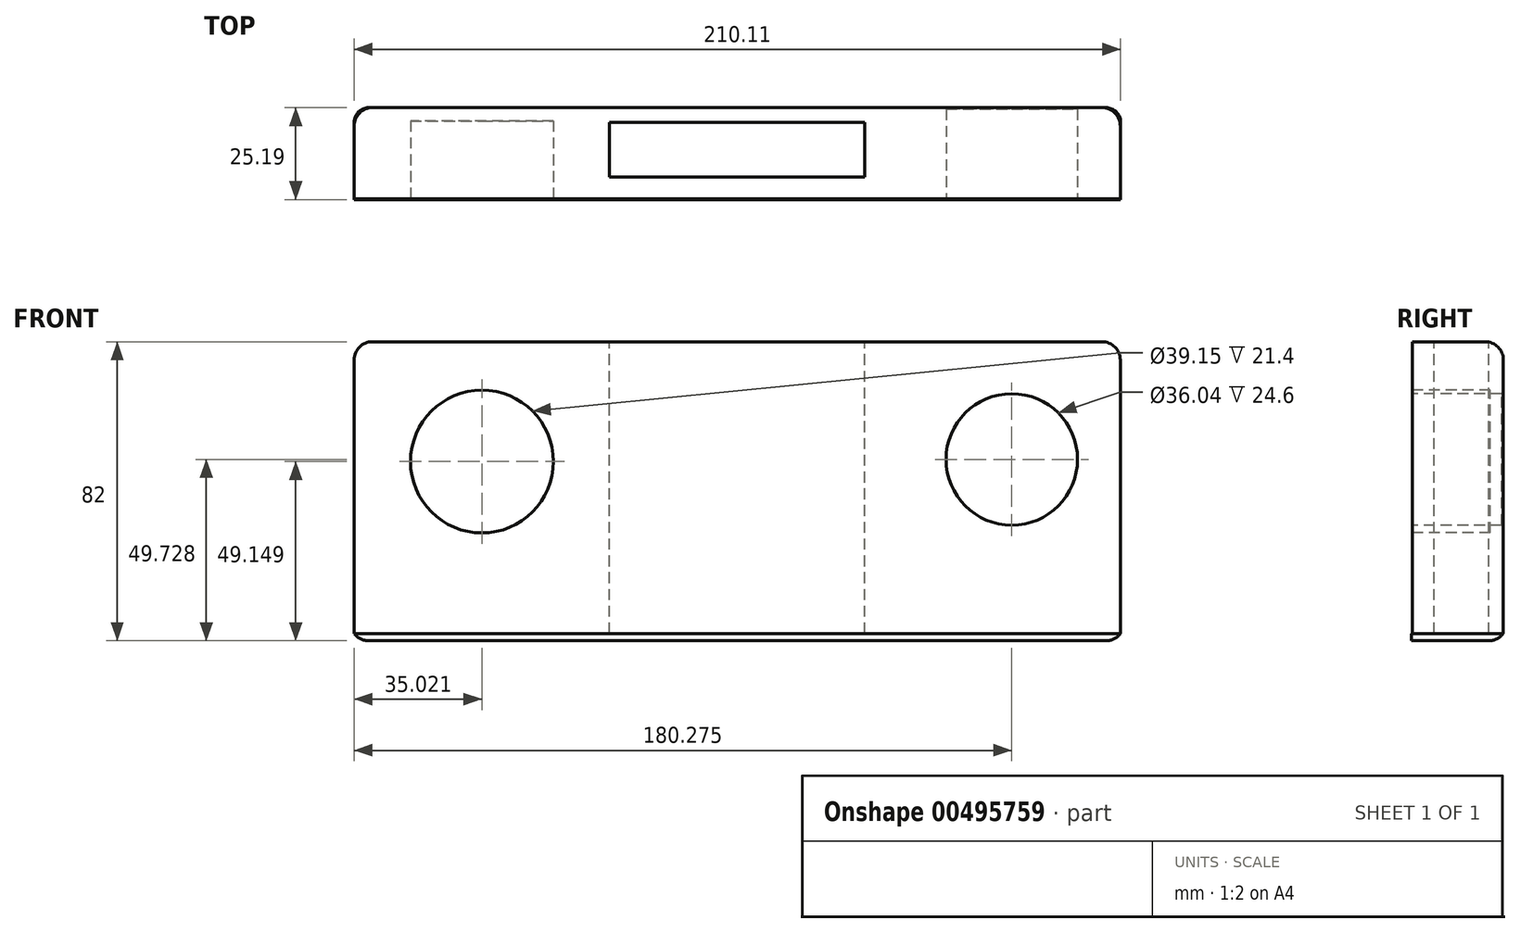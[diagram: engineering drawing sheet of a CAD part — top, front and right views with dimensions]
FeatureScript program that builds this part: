
annotation { "Feature Type Name" : "Feature", "Feature Type Description" : "" }
export const myFeature = defineFeature(function(context is Context, id is Id, definition is map)
    precondition{}
    {
        {
            var Q0;
            Q0=qCreatedBy(makeId("Front.planeOp"),FACE);
            var sketch = newSketch(context, id + "F0", { "sketchPlane" : qUnion([Q0])});
            skLineSegment(sketch, "E0.bottom", {"start": v(-105, 40) * mm, "end": v(105, 40) * mm});
            skLineSegment(sketch, "E0.top", {"start": v(-105, -40) * mm, "end": v(105, -40) * mm});
            skLineSegment(sketch, "E0.left", {"start": v(-105, 40) * mm, "end": v(-105, -40) * mm});
            skLineSegment(sketch, "E0.right", {"start": v(105, 40) * mm, "end": v(105, -40) * mm});
            skPoint(sketch, "E0.middle", {"position": v(0, 0) * mm});
            skSolve(sketch);
        }
        {
            var Q0;
            Q0 = qSketchRegion(id + "F0", true);
            extrude(context, id + "F1", {"entities" : qUnion([Q0]), "depth" : 25 * mm});
        }
        {
            var Q0;
            Q0=makeQuery(id+"F1.opExtrude","SWEPT_FACE",FACE,{"disambiguationData":[OSD([sQuery(id+"F0.wireOp",EDGE,"E0.bottom")])]});
            var sketch = newSketch(context, id + "F2", { "sketchPlane" : qUnion([Q0])});
            skLineSegment(sketch, "E1.bottom", {"start": v(-35, -3.97) * mm, "end": v(35, -3.97) * mm});
            skLineSegment(sketch, "E1.top", {"start": v(-35, -18.97) * mm, "end": v(35, -18.97) * mm});
            skLineSegment(sketch, "E1.left", {"start": v(-35, -3.97) * mm, "end": v(-35, -18.97) * mm});
            skLineSegment(sketch, "E1.right", {"start": v(35, -3.97) * mm, "end": v(35, -18.97) * mm});
            skPoint(sketch, "E1.middle", {"position": v(0, -11.47) * mm});
            skPoint(sketch, "E1.middle.positionSnap0", {"position": v(0, 0) * mm});
            skPoint(sketch, "E1.centerSnap0", {"position": v(0, 0) * mm});
            skSolve(sketch);
        }
        {
            var Q0;
            Q0 = qSketchRegion(id + "F2", true);
            extrude(context, id + "F3", {"entities" : qUnion([Q0]), "operationType" : NewBodyOperationType.REMOVE, "oppositeDirection" : true, "depth" : 111.1 * mm});
        }
        {
            var Q0;
            Q0=makeQuery(id+"F1.opExtrude","SWEPT_FACE",FACE,{"disambiguationData":[OSD([sQuery(id+"F0.wireOp",EDGE,"E0.top")])]});
            var sketch = newSketch(context, id + "F4", { "sketchPlane" : qUnion([Q0])});
            skSolve(sketch);
        }
        {
            var Q0;
            Q0=makeQuery(id+"F1.opExtrude","CAP_FACE",FACE,{"disambiguationData":[OSD([sQuery(id+"F0.wireOp",EDGE,"E0.bottom"),sQuery(id+"F0.wireOp",EDGE,"E0.top"),sQuery(id+"F0.wireOp",EDGE,"E0.left"),sQuery(id+"F0.wireOp",EDGE,"E0.right")])],"isStart":false});
            var sketch = newSketch(context, id + "F5", { "sketchPlane" : qUnion([Q0])});
            skCircle(sketch, "E2", {"center": v(-69.98, 7.15) * mm, "radius": 19.57 * mm});
            skPoint(sketch, "E2.first.point", {"position": v(-84.96, -5.44) * mm});
            skPoint(sketch, "E2.second.point", {"position": v(-52.58, 16.12) * mm});
            skPoint(sketch, "E2.third.point", {"position": v(-57.55, -7.97) * mm});
            skSolve(sketch);
        }
        {
            var Q0;
            Q0 = qSketchRegion(id + "F5", true);
            extrude(context, id + "F6", {"entities" : qUnion([Q0]), "operationType" : NewBodyOperationType.REMOVE, "oppositeDirection" : true, "depth" : 21.4 * mm});
        }
        {
            var Q0;
            Q0=makeQuery(id+"F1.opExtrude","CAP_FACE",FACE,{"disambiguationData":[OSD([sQuery(id+"F0.wireOp",EDGE,"E0.bottom"),sQuery(id+"F0.wireOp",EDGE,"E0.top"),sQuery(id+"F0.wireOp",EDGE,"E0.left"),sQuery(id+"F0.wireOp",EDGE,"E0.right")])],"isStart":false});
            var sketch = newSketch(context, id + "F7", { "sketchPlane" : qUnion([Q0])});
            skCircle(sketch, "E3", {"center": v(75.27, 7.73) * mm, "radius": 18.02 * mm});
            skPoint(sketch, "E3.first.point", {"position": v(59, 0) * mm});
            skPoint(sketch, "E3.second.point", {"position": v(88.16, 20.33) * mm});
            skPoint(sketch, "E3.third.point", {"position": v(82.38, -8.83) * mm});
            skSolve(sketch);
        }
        {
            var Q0;
            Q0 = qSketchRegion(id + "F7", true);
            extrude(context, id + "F8", {"entities" : qUnion([Q0]), "operationType" : NewBodyOperationType.REMOVE, "oppositeDirection" : true, "depth" : 24.6 * mm});
        }
        {
            var Q0;
            {var subQ0=sQuery(id+"F0.wireOp",EDGE,"E0.top");Q0=makeQuery(id+"F4.imprint","IMPRINT",FACE,{"disambiguationData":[TD([[makeQuery(id+"F4.imprint","IMPRINT",EDGE,{"derivedFrom":makeQuery(id+"F1.opExtrude","CAP_EDGE",EDGE,{"disambiguationData":[OSD([subQ0])],"isStart":true})}),1.0]])]});}
            var sketch = newSketch(context, id + "F9", { "sketchPlane" : qUnion([Q0])});
            skLineSegment(sketch, "E4.bottom", {"start": v(-104.98, 25.2) * mm, "end": v(105.11, 25.2) * mm});
            skLineSegment(sketch, "E4.top", {"start": v(-104.98, 0) * mm, "end": v(105.11, 0) * mm});
            skLineSegment(sketch, "E4.left", {"start": v(-104.98, 25.2) * mm, "end": v(-104.98, 0) * mm});
            skLineSegment(sketch, "E4.right", {"start": v(105.11, 25.2) * mm, "end": v(105.11, 0) * mm});
            skSolve(sketch);
        }
        {
            var Q0;
            Q0 = qSketchRegion(id + "F9", true);
            extrude(context, id + "F10", {"entities" : qUnion([Q0]), "depth" : 2 * mm});
        }
        {
            var Q0;
            Q0=makeQuery(id+"F1.opExtrude","SWEPT_EDGE",EDGE,{"disambiguationData":[OSD([sQuery(id+"F0.wireOp",EDGE,"E0.bottom"),sQuery(id+"F0.wireOp",EDGE,"E0.left")])]});
            var Q1;
            Q1=makeQuery(id+"F1.opExtrude","SWEPT_EDGE",EDGE,{"disambiguationData":[OSD([sQuery(id+"F0.wireOp",EDGE,"E0.bottom"),sQuery(id+"F0.wireOp",EDGE,"E0.right")])]});
            var Q2;
            Q2=makeQuery(id+"F10.opExtrude","CAP_EDGE",EDGE,{"disambiguationData":[OSD([sQuery(id+"F9.wireOp",EDGE,"E4.left")])],"isStart":false});
            var Q3;
            Q3=makeQuery(id+"F10.opExtrude","CAP_EDGE",EDGE,{"disambiguationData":[OSD([sQuery(id+"F9.wireOp",EDGE,"E4.right")])],"isStart":false});
            var Q4;
            Q4=makeQuery(id+"F1.opExtrude","CAP_EDGE",EDGE,{"disambiguationData":[OSD([sQuery(id+"F0.wireOp",EDGE,"E0.left")])],"isStart":true});
            var Q5;
            Q5=makeQuery(id+"F1.opExtrude","CAP_EDGE",EDGE,{"disambiguationData":[OSD([sQuery(id+"F0.wireOp",EDGE,"E0.right")])],"isStart":true});
            var Q6;
            Q6=makeQuery(id+"F10.opExtrude","CAP_EDGE",EDGE,{"disambiguationData":[OSD([sQuery(id+"F9.wireOp",EDGE,"E4.top")])],"isStart":false});
            var Q7;
            Q7=makeQuery(id+"F1.opExtrude","CAP_EDGE",EDGE,{"disambiguationData":[OSD([sQuery(id+"F0.wireOp",EDGE,"E0.bottom")])],"isStart":true});
            fillet(context, id + "F11", {"entities" : qUnion([Q0, Q1, Q2, Q3, Q4, Q5, Q6, Q7]), "radius" : 5 * mm, "tangentPropagation" : true, "allowEdgeOverflow" : false});
        }
        {
            var Q0;
            Q0=makeQuery(id+"F11.opFillet","BLEND_EDGE",EDGE,{"blendedFrom":[makeQuery(id+"F10.opExtrude","CAP_EDGE",EDGE,{"disambiguationData":[OSD([sQuery(id+"F9.wireOp",EDGE,"E4.top")])],"isStart":false}),makeQuery(id+"F10.opExtrude","CAP_EDGE",EDGE,{"disambiguationData":[OSD([sQuery(id+"F9.wireOp",EDGE,"E4.left")])],"isStart":false})],"blendedInto":[]});
            var Q1;
            Q1=makeQuery(id+"F11.opFillet","BLEND_EDGE",EDGE,{"blendedFrom":[makeQuery(id+"F10.opExtrude","CAP_EDGE",EDGE,{"disambiguationData":[OSD([sQuery(id+"F9.wireOp",EDGE,"E4.top")])],"isStart":false}),makeQuery(id+"F10.opExtrude","CAP_EDGE",EDGE,{"disambiguationData":[OSD([sQuery(id+"F9.wireOp",EDGE,"E4.right")])],"isStart":false})],"blendedInto":[]});
            fillet(context, id + "F12", {"entities" : qUnion([Q0, Q1]), "radius" : 5 * mm, "tangentPropagation" : true, "allowEdgeOverflow" : false});
        }
    });
